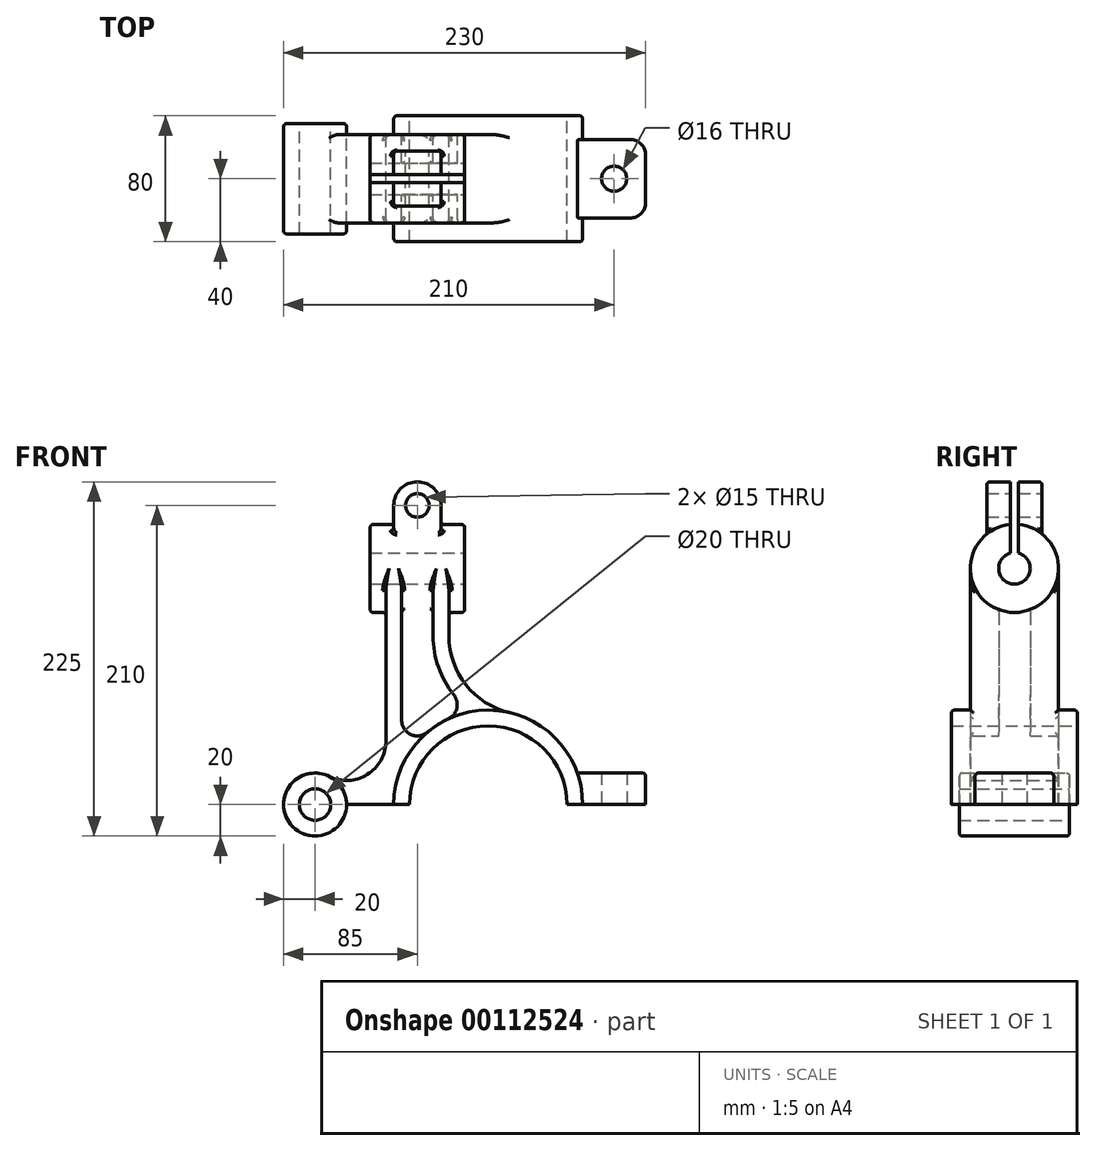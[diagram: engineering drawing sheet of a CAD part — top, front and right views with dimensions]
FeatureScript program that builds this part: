
annotation { "Feature Type Name" : "Feature", "Feature Type Description" : "" }
export const myFeature = defineFeature(function(context is Context, id is Id, definition is map)
    precondition{}
    {
        {
            var Q0;
            Q0=qCreatedBy(makeId("Front.planeOp"),FACE);
            var sketch = newSketch(context, id + "F0", { "sketchPlane" : qUnion([Q0])});
            skLineSegment(sketch, "E0", {"start": v(100, 0) * mm, "end": v(-90, 0) * mm});
            skArc(sketch, "E1", {"start": v(50, 0) * mm, "mid": v(0, 50) * mm, "end": v(-50, 0) * mm});
            skArc(sketch, "E2", {"start": v(60, 0) * mm, "mid": v(0, 60) * mm, "end": v(-60, 0) * mm});
            skLineSegment(sketch, "E3", {"start": v(56.57, 20) * mm, "end": v(100, 20) * mm});
            skLineSegment(sketch, "E4", {"start": v(100, 20) * mm, "end": v(100, 0) * mm});
            skLineSegment(sketch, "E5", {"start": v(80, 20) * mm, "end": v(80, 0) * mm});
            skCircle(sketch, "E6", {"center": v(-110, 0) * mm, "radius": 20 * mm});
            skCircle(sketch, "E7", {"center": v(-110, 0) * mm, "radius": 10 * mm});
            skLineSegment(sketch, "E8", {"start": v(-75, 150) * mm, "end": v(-15, 150) * mm});
            skLineSegment(sketch, "E9", {"start": v(-65, 150) * mm, "end": v(-65, 40.31) * mm});
            skArc(sketch, "E10", {"start": v(-101.11, 17.92) * mm, "mid": v(-76.82, 19.07) * mm, "end": v(-65, 40.31) * mm});
            skLineSegment(sketch, "E11", {"start": v(-25, 150) * mm, "end": v(-25, 107.12) * mm});
            skArc(sketch, "E12", {"start": v(-25, 107.12) * mm, "mid": v(-14.17, 76.04) * mm, "end": v(13.64, 58.43) * mm});
            skLineSegment(sketch, "E13", {"start": v(-35, 150) * mm, "end": v(-35, 107.12) * mm});
            skLineSegment(sketch, "E14", {"start": v(-55, 150) * mm, "end": v(-55, 53.62) * mm});
            skArc(sketch, "E15", {"start": v(-35, 107.12) * mm, "mid": v(-31.62, 87.27) * mm, "end": v(-21.86, 69.65) * mm});
            skArc(sketch, "E16", {"start": v(-55, 53.62) * mm, "mid": v(-49.23, 44.56) * mm, "end": v(-38.57, 45.96) * mm});
            skArc(sketch, "E17", {"start": v(-25.43, 54.34) * mm, "mid": v(-19.93, 61.13) * mm, "end": v(-21.86, 69.65) * mm});
            skLineSegment(sketch, "E18", {"start": v(-75, 178) * mm, "end": v(-75, 122) * mm});
            skLineSegment(sketch, "E19", {"start": v(-75, 122) * mm, "end": v(-15, 122) * mm});
            skLineSegment(sketch, "E20", {"start": v(-15, 122) * mm, "end": v(-15, 178) * mm});
            skLineSegment(sketch, "E21", {"start": v(-15, 178) * mm, "end": v(-75, 178) * mm});
            skLineSegment(sketch, "E22", {"start": v(88, 20) * mm, "end": v(88, 0) * mm});
            skLineSegment(sketch, "E23", {"start": v(-60, 155) * mm, "end": v(-30, 155) * mm});
            skLineSegment(sketch, "E24", {"start": v(-30, 155) * mm, "end": v(-30, 190) * mm});
            skArc(sketch, "E25", {"start": v(-30, 190) * mm, "mid": v(-45, 205) * mm, "end": v(-60, 190) * mm});
            skLineSegment(sketch, "E26", {"start": v(-60, 190) * mm, "end": v(-60, 155) * mm});
            skCircle(sketch, "E27", {"center": v(-45, 190) * mm, "radius": 7.5 * mm});
            skSolve(sketch);
        }
        {
            var Q0;
            {var subQ4=sQuery(id+"F0.wireOp",EDGE,"E1");Q0=makeQuery(id+"F0.imprint","IMPRINT",FACE,{"disambiguationData":[TD([[makeQuery(id+"F0.imprint","IMPRINT",EDGE,{"derivedFrom":subQ4}),-1.0]])]});}
            extrude(context, id + "F1", {"entities" : qUnion([Q0]), "endBound" : BoundingType.SYMMETRIC, "depth" : 80 * mm});
        }
        {
            var Q0;
            Q0=makeQuery(id+"F0.imprint","IMPRINT",FACE,{"disambiguationData":[TD([[makeQuery(id+"F0.imprint","IMPRINT",EDGE,{"derivedFrom":sQuery(id+"F0.wireOp",EDGE,"E7")}),-1.0]])]});
            extrude(context, id + "F2", {"entities" : qUnion([Q0]), "operationType" : NewBodyOperationType.ADD, "endBound" : BoundingType.SYMMETRIC, "depth" : 70 * mm});
        }
        {
            var Q0;
            {var subQ3=sQuery(id+"F0.wireOp",EDGE,"E5");Q0=makeQuery(id+"F0.imprint","IMPRINT",FACE,{"disambiguationData":[TD([[makeQuery(id+"F0.imprint","IMPRINT",EDGE,{"derivedFrom":subQ3}),-1.0]])]});}
            var Q1;
            {var subQ0=sQuery(id+"F0.wireOp",EDGE,"E5");Q1=makeQuery(id+"F0.imprint","IMPRINT",FACE,{"disambiguationData":[TD([[makeQuery(id+"F0.imprint","IMPRINT",EDGE,{"derivedFrom":subQ0}),1.0]])]});}
            var Q2;
            {var subQ0=sQuery(id+"F0.wireOp",EDGE,"E4");Q2=makeQuery(id+"F0.imprint","IMPRINT",FACE,{"disambiguationData":[TD([[makeQuery(id+"F0.imprint","IMPRINT",EDGE,{"derivedFrom":subQ0}),-1.0]])]});}
            extrude(context, id + "F3", {"entities" : qUnion([Q0, Q1, Q2]), "operationType" : NewBodyOperationType.ADD, "endBound" : BoundingType.SYMMETRIC, "depth" : 50 * mm});
        }
        {
            var Q0;
            {var subQ0=sQuery(id+"F0.wireOp",EDGE,"E5");Q0=makeQuery(id+"F0.imprint","IMPRINT",FACE,{"disambiguationData":[TD([[makeQuery(id+"F0.imprint","IMPRINT",EDGE,{"derivedFrom":subQ0}),1.0]])]});}
            var Q1;
            Q1=sQuery(id+"F0.wireOp",EDGE,"E5");
            revolve(context, id + "F4", {"operationType" : NewBodyOperationType.REMOVE, "entities" : qUnion([Q0]), "axis" : qUnion([Q1]), "revolveType" : RevolveType.FULL, "oppositeDirection" : true});
        }
        {
            var Q0;
            Q0=makeQuery(id+"F3.opExtrude","CAP_EDGE",EDGE,{"disambiguationData":[OSD([sQuery(id+"F0.wireOp",EDGE,"E4")])],"isStart":false});
            var Q1;
            Q1=makeQuery(id+"F3.opExtrude","CAP_EDGE",EDGE,{"disambiguationData":[OSD([sQuery(id+"F0.wireOp",EDGE,"E4")])],"isStart":true});
            fillet(context, id + "F5", {"entities" : qUnion([Q0, Q1]), "radius" : 10 * mm, "tangentPropagation" : true, "allowEdgeOverflow" : false});
        }
        {
            var Q0;
            {var subQ3=sQuery(id+"F0.wireOp",EDGE,"E10");Q0=makeQuery(id+"F0.imprint","IMPRINT",FACE,{"disambiguationData":[TD([[makeQuery(id+"F0.imprint","IMPRINT",EDGE,{"derivedFrom":subQ3}),-1.0]])]});}
            var Q1;
            {var subQ0=sQuery(id+"F0.wireOp",EDGE,"E9");var subQ1=sQuery(id+"F0.wireOp",EDGE,"E8");var subQ2=makeQuery(id+"F0.imprint","INTERSECT",VERTEX,{"derivedFrom":[subQ1,subQ0]});Q1=makeQuery(id+"F0.imprint","IMPRINT",FACE,{"disambiguationData":[TD([[makeQuery(id+"F0.imprint","IMPRINT",EDGE,{"disambiguationData":[TD([[subQ2,-1.0]])],"derivedFrom":subQ1}),-1.0]])]});}
            var Q2;
            {var subQ0=sQuery(id+"F0.wireOp",EDGE,"E11");var subQ1=sQuery(id+"F0.wireOp",EDGE,"E8");var subQ2=makeQuery(id+"F0.imprint","INTERSECT",VERTEX,{"derivedFrom":[subQ1,subQ0]});Q2=makeQuery(id+"F0.imprint","IMPRINT",FACE,{"disambiguationData":[TD([[makeQuery(id+"F0.imprint","IMPRINT",EDGE,{"disambiguationData":[TD([[subQ2,1.0]])],"derivedFrom":subQ1}),-1.0]])]});}
            var Q3;
            {var subQ4=sQuery(id+"F0.wireOp",EDGE,"E12");Q3=makeQuery(id+"F0.imprint","IMPRINT",FACE,{"disambiguationData":[TD([[makeQuery(id+"F0.imprint","IMPRINT",EDGE,{"derivedFrom":subQ4}),-1.0]])]});}
            extrude(context, id + "F6", {"entities" : qUnion([Q0, Q1, Q2, Q3]), "operationType" : NewBodyOperationType.ADD, "endBound" : BoundingType.SYMMETRIC, "depth" : 56 * mm});
        }
        {
            var Q0;
            {var subQ0=sQuery(id+"F0.wireOp",EDGE,"E15");Q0=makeQuery(id+"F0.imprint","IMPRINT",FACE,{"disambiguationData":[TD([[makeQuery(id+"F0.imprint","IMPRINT",EDGE,{"derivedFrom":subQ0}),-1.0]])]});}
            var Q1;
            {var subQ0=sQuery(id+"F0.wireOp",EDGE,"E13");var subQ1=sQuery(id+"F0.wireOp",EDGE,"E8");var subQ2=makeQuery(id+"F0.imprint","INTERSECT",VERTEX,{"derivedFrom":[subQ1,subQ0]});Q1=makeQuery(id+"F0.imprint","IMPRINT",FACE,{"disambiguationData":[TD([[makeQuery(id+"F0.imprint","IMPRINT",EDGE,{"disambiguationData":[TD([[subQ2,1.0]])],"derivedFrom":subQ1}),-1.0]])]});}
            extrude(context, id + "F7", {"entities" : qUnion([Q0, Q1]), "operationType" : NewBodyOperationType.ADD, "endBound" : BoundingType.SYMMETRIC, "depth" : 20 * mm});
        }
        {
            var Q0;
            {var subQ11=sQuery(id+"F0.wireOp",EDGE,"E23");Q0=makeQuery(id+"F0.imprint","IMPRINT",FACE,{"disambiguationData":[TD([[makeQuery(id+"F0.imprint","IMPRINT",EDGE,{"derivedFrom":subQ11}),-1.0]])]});}
            var Q1;
            {var subQ5=sQuery(id+"F0.wireOp",EDGE,"E23");Q1=makeQuery(id+"F0.imprint","IMPRINT",FACE,{"disambiguationData":[TD([[makeQuery(id+"F0.imprint","IMPRINT",EDGE,{"derivedFrom":subQ5}),1.0]])]});}
            var Q2;
            Q2=sQuery(id+"F0.wireOp",EDGE,"E8");
            revolve(context, id + "F8", {"operationType" : NewBodyOperationType.ADD, "entities" : qUnion([Q0, Q1]), "axis" : qUnion([Q2]), "revolveType" : RevolveType.FULL});
        }
        {
            var Q0;
            {var subQ1=sQuery(id+"F0.wireOp",EDGE,"E25");Q0=makeQuery(id+"F0.imprint","IMPRINT",FACE,{"disambiguationData":[TD([[makeQuery(id+"F0.imprint","IMPRINT",EDGE,{"derivedFrom":subQ1}),1.0]])]});}
            var Q1;
            {var subQ5=sQuery(id+"F0.wireOp",EDGE,"E23");Q1=makeQuery(id+"F0.imprint","IMPRINT",FACE,{"disambiguationData":[TD([[makeQuery(id+"F0.imprint","IMPRINT",EDGE,{"derivedFrom":subQ5}),1.0]])]});}
            extrude(context, id + "F9", {"entities" : qUnion([Q0, Q1]), "operationType" : NewBodyOperationType.ADD, "endBound" : BoundingType.SYMMETRIC, "depth" : 35 * mm});
        }
        {
            var Q0;
            Q0=makeQuery(id+"F8.opRevolve","SWEPT_FACE",FACE,{"disambiguationData":[OSD([sQuery(id+"F0.wireOp",EDGE,"E20")])]});
            var sketch = newSketch(context, id + "F10", { "sketchPlane" : qUnion([Q0])});
            skCircle(sketch, "E28", {"center": v(0, 150) * mm, "radius": 10 * mm});
            skSolve(sketch);
        }
        {
            var Q0;
            Q0 = qSketchRegion(id + "F10", true);
            extrude(context, id + "F11", {"entities" : qUnion([Q0]), "operationType" : NewBodyOperationType.REMOVE, "endBound" : BoundingType.UP_TO_NEXT, "oppositeDirection" : true, "depth" : 25 * mm});
        }
        {
            var Q0;
            {var subQ5=sQuery(id+"F0.wireOp",EDGE,"E23");Q0=makeQuery(id+"F0.imprint","IMPRINT",FACE,{"disambiguationData":[TD([[makeQuery(id+"F0.imprint","IMPRINT",EDGE,{"derivedFrom":subQ5}),1.0]])]});}
            var Q1;
            {var subQ1=sQuery(id+"F0.wireOp",EDGE,"E25");Q1=makeQuery(id+"F0.imprint","IMPRINT",FACE,{"disambiguationData":[TD([[makeQuery(id+"F0.imprint","IMPRINT",EDGE,{"derivedFrom":subQ1}),1.0]])]});}
            var Q2;
            {var subQ11=sQuery(id+"F0.wireOp",EDGE,"E23");Q2=makeQuery(id+"F0.imprint","IMPRINT",FACE,{"disambiguationData":[TD([[makeQuery(id+"F0.imprint","IMPRINT",EDGE,{"derivedFrom":subQ11}),-1.0]])]});}
            extrude(context, id + "F12", {"entities" : qUnion([Q0, Q1, Q2]), "operationType" : NewBodyOperationType.REMOVE, "endBound" : BoundingType.SYMMETRIC, "oppositeDirection" : true, "depth" : 5 * mm});
        }
        {
            var Q0;
            Q0=makeQuery(id+"F7.opExtrude","CAP_EDGE",EDGE,{"disambiguationData":[OSD([sQuery(id+"F0.wireOp",EDGE,"E14")])],"isStart":false});
            var Q1;
            Q1=makeQuery(id+"F8.boolean.opBoolean","INTERSECT",EDGE,{"derivedFrom":[makeQuery(id+"F7.opExtrude","CAP_FACE",FACE,{"disambiguationData":[OSD([sQuery(id+"F0.wireOp",EDGE,"E2"),sQuery(id+"F0.wireOp",EDGE,"E8"),sQuery(id+"F0.wireOp",EDGE,"E13"),sQuery(id+"F0.wireOp",EDGE,"E14"),sQuery(id+"F0.wireOp",EDGE,"E15"),sQuery(id+"F0.wireOp",EDGE,"E16"),sQuery(id+"F0.wireOp",EDGE,"E17")])],"isStart":false}),makeQuery(id+"F8.opRevolve","SWEPT_FACE",FACE,{"disambiguationData":[OSD([sQuery(id+"F0.wireOp",EDGE,"E21")])]})]});
            var Q2;
            {var subQ0=sQuery(id+"F0.wireOp",EDGE,"E15");var subQ1=sQuery(id+"F0.wireOp",EDGE,"E11");var subQ2=sQuery(id+"F0.wireOp",EDGE,"E8");var subQ3=sQuery(id+"F0.wireOp",EDGE,"E13");var subQ5=sQuery(id+"F0.wireOp",EDGE,"E17");var subQ6=sQuery(id+"F0.wireOp",EDGE,"E2");Q2=makeQuery(id+"F8.boolean.opBoolean","INTERSECT",EDGE,{"derivedFrom":[makeQuery(id+"F7.boolean.opBoolean","SPLIT",FACE,{"disambiguationData":[TD([makeQuery(id+"F6.opExtrude","CAP_FACE",FACE,{"disambiguationData":[OSD([subQ6,subQ2,subQ1,sQuery(id+"F0.wireOp",EDGE,"E12"),subQ3,subQ0,subQ5])],"isStart":false})])],"derivedFrom":makeQuery(id+"F6.opExtrude","SWEPT_FACE",FACE,{"disambiguationData":[OSD([subQ3])]})}),makeQuery(id+"F8.opRevolve","SWEPT_FACE",FACE,{"disambiguationData":[OSD([sQuery(id+"F0.wireOp",EDGE,"E21")])]})]});}
            var Q3;
            {var subQ0=sQuery(id+"F0.wireOp",EDGE,"E16");var subQ1=sQuery(id+"F0.wireOp",EDGE,"E8");var subQ2=sQuery(id+"F0.wireOp",EDGE,"E13");var subQ3=sQuery(id+"F0.wireOp",EDGE,"E14");var subQ5=sQuery(id+"F0.wireOp",EDGE,"E2");Q3=makeQuery(id+"F8.boolean.opBoolean","INTERSECT",EDGE,{"derivedFrom":[makeQuery(id+"F7.boolean.opBoolean","SPLIT",FACE,{"disambiguationData":[TD([makeQuery(id+"F7.opExtrude","CAP_FACE",FACE,{"disambiguationData":[OSD([subQ5,subQ1,subQ2,subQ3,sQuery(id+"F0.wireOp",EDGE,"E15"),subQ0,sQuery(id+"F0.wireOp",EDGE,"E17")])],"isStart":false})])],"derivedFrom":makeQuery(id+"F6.opExtrude","SWEPT_FACE",FACE,{"disambiguationData":[OSD([subQ3])]})}),makeQuery(id+"F8.opRevolve","SWEPT_FACE",FACE,{"disambiguationData":[OSD([sQuery(id+"F0.wireOp",EDGE,"E21")])]})]});}
            var Q4;
            Q4=makeQuery(id+"F8.boolean.opBoolean","INTERSECT",EDGE,{"derivedFrom":[makeQuery(id+"F6.opExtrude","SWEPT_FACE",FACE,{"disambiguationData":[OSD([sQuery(id+"F0.wireOp",EDGE,"E9")])]}),makeQuery(id+"F8.opRevolve","SWEPT_FACE",FACE,{"disambiguationData":[OSD([sQuery(id+"F0.wireOp",EDGE,"E21")])]})]});
            var Q5;
            Q5=makeQuery(id+"F8.boolean.opBoolean","INTERSECT",EDGE,{"derivedFrom":[makeQuery(id+"F6.opExtrude","SWEPT_FACE",FACE,{"disambiguationData":[OSD([sQuery(id+"F0.wireOp",EDGE,"E11")])]}),makeQuery(id+"F8.opRevolve","SWEPT_FACE",FACE,{"disambiguationData":[OSD([sQuery(id+"F0.wireOp",EDGE,"E21")])]})]});
            var Q6;
            {var subQ0=sQuery(id+"F0.wireOp",EDGE,"E2");Q6=makeQuery(id+"F6.opExtrude","CAP_EDGE",EDGE,{"disambiguationData":[OSD([subQ0]),TDD([makeQuery(id+"F0.imprint","IMPRINT",EDGE,{"disambiguationData":[TD([[makeQuery(id+"F0.imprint","INTERSECT",VERTEX,{"derivedFrom":[subQ0,sQuery(id+"F0.wireOp",EDGE,"E12")]}),-1.0]])],"derivedFrom":subQ0})])],"isStart":false});}
            var Q7;
            {var subQ0=sQuery(id+"F0.wireOp",EDGE,"E2");Q7=makeQuery(id+"F6.opExtrude","CAP_EDGE",EDGE,{"disambiguationData":[OSD([subQ0]),TDD([makeQuery(id+"F0.imprint","IMPRINT",EDGE,{"disambiguationData":[TD([[makeQuery(id+"F0.imprint","INTERSECT",VERTEX,{"disambiguationData":[OD(1.0)],"derivedFrom":[sQuery(id+"F0.wireOp",EDGE,"E0"),subQ0]}),1.0]])],"derivedFrom":subQ0})])],"isStart":false});}
            var Q8;
            {var subQ0=sQuery(id+"F0.wireOp",EDGE,"E2");Q8=makeQuery(id+"F6.opExtrude","CAP_EDGE",EDGE,{"disambiguationData":[OSD([subQ0]),TDD([makeQuery(id+"F0.imprint","IMPRINT",EDGE,{"disambiguationData":[TD([[makeQuery(id+"F0.imprint","INTERSECT",VERTEX,{"derivedFrom":[subQ0,sQuery(id+"F0.wireOp",EDGE,"E12")]}),-1.0]])],"derivedFrom":subQ0})])],"isStart":true});}
            var Q9;
            {var subQ0=sQuery(id+"F0.wireOp",EDGE,"E2");Q9=makeQuery(id+"F6.opExtrude","CAP_EDGE",EDGE,{"disambiguationData":[OSD([subQ0]),TDD([makeQuery(id+"F0.imprint","IMPRINT",EDGE,{"disambiguationData":[TD([[makeQuery(id+"F0.imprint","INTERSECT",VERTEX,{"disambiguationData":[OD(1.0)],"derivedFrom":[sQuery(id+"F0.wireOp",EDGE,"E0"),subQ0]}),1.0]])],"derivedFrom":subQ0})])],"isStart":true});}
            var Q10;
            Q10=makeQuery(id+"F7.opExtrude","CAP_EDGE",EDGE,{"disambiguationData":[OSD([sQuery(id+"F0.wireOp",EDGE,"E2")])],"isStart":true});
            var Q11;
            Q11=makeQuery(id+"F8.boolean.opBoolean","INTERSECT",EDGE,{"derivedFrom":[makeQuery(id+"F7.opExtrude","CAP_FACE",FACE,{"disambiguationData":[OSD([sQuery(id+"F0.wireOp",EDGE,"E2"),sQuery(id+"F0.wireOp",EDGE,"E8"),sQuery(id+"F0.wireOp",EDGE,"E13"),sQuery(id+"F0.wireOp",EDGE,"E14"),sQuery(id+"F0.wireOp",EDGE,"E15"),sQuery(id+"F0.wireOp",EDGE,"E16"),sQuery(id+"F0.wireOp",EDGE,"E17")])],"isStart":true}),makeQuery(id+"F8.opRevolve","SWEPT_FACE",FACE,{"disambiguationData":[OSD([sQuery(id+"F0.wireOp",EDGE,"E21")])]})]});
            var Q12;
            {var subQ0=sQuery(id+"F0.wireOp",EDGE,"E16");var subQ1=sQuery(id+"F0.wireOp",EDGE,"E8");var subQ2=sQuery(id+"F0.wireOp",EDGE,"E13");var subQ4=sQuery(id+"F0.wireOp",EDGE,"E14");var subQ5=sQuery(id+"F0.wireOp",EDGE,"E2");Q12=makeQuery(id+"F8.boolean.opBoolean","INTERSECT",EDGE,{"derivedFrom":[makeQuery(id+"F7.boolean.opBoolean","SPLIT",FACE,{"disambiguationData":[TD([makeQuery(id+"F7.opExtrude","CAP_FACE",FACE,{"disambiguationData":[OSD([subQ5,subQ1,subQ2,subQ4,sQuery(id+"F0.wireOp",EDGE,"E15"),subQ0,sQuery(id+"F0.wireOp",EDGE,"E17")])],"isStart":true})])],"derivedFrom":makeQuery(id+"F6.opExtrude","SWEPT_FACE",FACE,{"disambiguationData":[OSD([subQ4])]})}),makeQuery(id+"F8.opRevolve","SWEPT_FACE",FACE,{"disambiguationData":[OSD([sQuery(id+"F0.wireOp",EDGE,"E21")])]})]});}
            var Q13;
            {var subQ0=sQuery(id+"F0.wireOp",EDGE,"E15");var subQ1=sQuery(id+"F0.wireOp",EDGE,"E11");var subQ2=sQuery(id+"F0.wireOp",EDGE,"E8");var subQ3=sQuery(id+"F0.wireOp",EDGE,"E13");var subQ5=sQuery(id+"F0.wireOp",EDGE,"E17");var subQ6=sQuery(id+"F0.wireOp",EDGE,"E2");Q13=makeQuery(id+"F8.boolean.opBoolean","INTERSECT",EDGE,{"derivedFrom":[makeQuery(id+"F7.boolean.opBoolean","SPLIT",FACE,{"disambiguationData":[TD([makeQuery(id+"F6.opExtrude","CAP_FACE",FACE,{"disambiguationData":[OSD([subQ6,subQ2,subQ1,sQuery(id+"F0.wireOp",EDGE,"E12"),subQ3,subQ0,subQ5])],"isStart":true})])],"derivedFrom":makeQuery(id+"F6.opExtrude","SWEPT_FACE",FACE,{"disambiguationData":[OSD([subQ3])]})}),makeQuery(id+"F8.opRevolve","SWEPT_FACE",FACE,{"disambiguationData":[OSD([sQuery(id+"F0.wireOp",EDGE,"E21")])]})]});}
            var Q14;
            Q14=makeQuery(id+"F6.opExtrude","CAP_EDGE",EDGE,{"disambiguationData":[OSD([sQuery(id+"F0.wireOp",EDGE,"E6")])],"isStart":true});
            var Q15;
            Q15=makeQuery(id+"F6.opExtrude","CAP_EDGE",EDGE,{"disambiguationData":[OSD([sQuery(id+"F0.wireOp",EDGE,"E6")])],"isStart":false});
            var Q16;
            Q16=makeQuery(id+"F6.opExtrude","SWEPT_EDGE",EDGE,{"disambiguationData":[OSD([sQuery(id+"F0.wireOp",EDGE,"E0"),sQuery(id+"F0.wireOp",EDGE,"E6")])]});
            var Q17;
            Q17=makeQuery(id+"F9.boolean.opBoolean","INTERSECT",EDGE,{"derivedFrom":[makeQuery(id+"F8.opRevolve","SWEPT_FACE",FACE,{"disambiguationData":[OSD([sQuery(id+"F0.wireOp",EDGE,"E21")])]}),makeQuery(id+"F9.opExtrude","CAP_FACE",FACE,{"disambiguationData":[OSD([sQuery(id+"F0.wireOp",EDGE,"E23"),sQuery(id+"F0.wireOp",EDGE,"E24"),sQuery(id+"F0.wireOp",EDGE,"E25"),sQuery(id+"F0.wireOp",EDGE,"E26"),sQuery(id+"F0.wireOp",EDGE,"E27")])],"isStart":true})]});
            var Q18;
            {var subQ0=sQuery(id+"F0.wireOp",EDGE,"E21");var subQ1=makeQuery(id+"F8.opRevolve","SWEPT_FACE",FACE,{"disambiguationData":[OSD([subQ0])]});var subQ2=sQuery(id+"F0.wireOp",EDGE,"E27");var subQ3=sQuery(id+"F0.wireOp",EDGE,"E26");var subQ4=sQuery(id+"F0.wireOp",EDGE,"E25");var subQ5=sQuery(id+"F0.wireOp",EDGE,"E24");var subQ6=makeQuery(id+"F9.opExtrude","SWEPT_FACE",FACE,{"disambiguationData":[OSD([subQ3])]});Q18=makeQuery(id+"F12.boolean.opBoolean","SPLIT",EDGE,{"disambiguationData":[TD([makeQuery(id+"F9.opExtrude","CAP_FACE",FACE,{"disambiguationData":[OSD([sQuery(id+"F0.wireOp",EDGE,"E23"),subQ5,subQ4,subQ3,subQ2])],"isStart":true})])],"derivedFrom":makeQuery(id+"F9.boolean.opBoolean","INTERSECT",EDGE,{"derivedFrom":[subQ1,subQ6]})});}
            var Q19;
            Q19=makeQuery(id+"F9.boolean.opBoolean","INTERSECT",EDGE,{"derivedFrom":[makeQuery(id+"F8.opRevolve","SWEPT_FACE",FACE,{"disambiguationData":[OSD([sQuery(id+"F0.wireOp",EDGE,"E21")])]}),makeQuery(id+"F9.opExtrude","CAP_FACE",FACE,{"disambiguationData":[OSD([sQuery(id+"F0.wireOp",EDGE,"E23"),sQuery(id+"F0.wireOp",EDGE,"E24"),sQuery(id+"F0.wireOp",EDGE,"E25"),sQuery(id+"F0.wireOp",EDGE,"E26"),sQuery(id+"F0.wireOp",EDGE,"E27")])],"isStart":false})]});
            var Q20;
            {var subQ0=sQuery(id+"F0.wireOp",EDGE,"E21");var subQ1=makeQuery(id+"F8.opRevolve","SWEPT_FACE",FACE,{"disambiguationData":[OSD([subQ0])]});var subQ2=sQuery(id+"F0.wireOp",EDGE,"E27");var subQ3=sQuery(id+"F0.wireOp",EDGE,"E26");var subQ4=sQuery(id+"F0.wireOp",EDGE,"E25");var subQ5=sQuery(id+"F0.wireOp",EDGE,"E24");var subQ6=makeQuery(id+"F9.opExtrude","SWEPT_FACE",FACE,{"disambiguationData":[OSD([subQ3])]});Q20=makeQuery(id+"F12.boolean.opBoolean","SPLIT",EDGE,{"disambiguationData":[TD([makeQuery(id+"F9.opExtrude","CAP_FACE",FACE,{"disambiguationData":[OSD([sQuery(id+"F0.wireOp",EDGE,"E23"),subQ5,subQ4,subQ3,subQ2])],"isStart":false})])],"derivedFrom":makeQuery(id+"F9.boolean.opBoolean","INTERSECT",EDGE,{"derivedFrom":[subQ1,subQ6]})});}
            var Q21;
            {var subQ0=sQuery(id+"F0.wireOp",EDGE,"E21");var subQ1=makeQuery(id+"F8.opRevolve","SWEPT_FACE",FACE,{"disambiguationData":[OSD([subQ0])]});var subQ2=sQuery(id+"F0.wireOp",EDGE,"E27");var subQ3=sQuery(id+"F0.wireOp",EDGE,"E26");var subQ4=sQuery(id+"F0.wireOp",EDGE,"E25");var subQ5=sQuery(id+"F0.wireOp",EDGE,"E24");var subQ6=makeQuery(id+"F9.opExtrude","SWEPT_FACE",FACE,{"disambiguationData":[OSD([subQ5])]});Q21=makeQuery(id+"F12.boolean.opBoolean","SPLIT",EDGE,{"disambiguationData":[TD([makeQuery(id+"F9.opExtrude","CAP_FACE",FACE,{"disambiguationData":[OSD([sQuery(id+"F0.wireOp",EDGE,"E23"),subQ5,subQ4,subQ3,subQ2])],"isStart":false})])],"derivedFrom":makeQuery(id+"F9.boolean.opBoolean","INTERSECT",EDGE,{"derivedFrom":[subQ1,subQ6]})});}
            var Q22;
            {var subQ0=sQuery(id+"F0.wireOp",EDGE,"E21");var subQ1=makeQuery(id+"F8.opRevolve","SWEPT_FACE",FACE,{"disambiguationData":[OSD([subQ0])]});var subQ2=sQuery(id+"F0.wireOp",EDGE,"E27");var subQ3=sQuery(id+"F0.wireOp",EDGE,"E26");var subQ4=sQuery(id+"F0.wireOp",EDGE,"E25");var subQ5=sQuery(id+"F0.wireOp",EDGE,"E24");var subQ6=makeQuery(id+"F9.opExtrude","SWEPT_FACE",FACE,{"disambiguationData":[OSD([subQ5])]});Q22=makeQuery(id+"F12.boolean.opBoolean","SPLIT",EDGE,{"disambiguationData":[TD([makeQuery(id+"F9.opExtrude","CAP_FACE",FACE,{"disambiguationData":[OSD([sQuery(id+"F0.wireOp",EDGE,"E23"),subQ5,subQ4,subQ3,subQ2])],"isStart":true})])],"derivedFrom":makeQuery(id+"F9.boolean.opBoolean","INTERSECT",EDGE,{"derivedFrom":[subQ1,subQ6]})});}
            var Q23;
            Q23=makeQuery(id+"F9.opExtrude","CAP_EDGE",EDGE,{"disambiguationData":[OSD([sQuery(id+"F0.wireOp",EDGE,"E24")])],"isStart":false});
            var Q24;
            Q24=makeQuery(id+"F9.opExtrude","CAP_EDGE",EDGE,{"disambiguationData":[OSD([sQuery(id+"F0.wireOp",EDGE,"E24")])],"isStart":true});
            var Q25;
            Q25=makeQuery(id+"F8.opRevolve","SWEPT_EDGE",EDGE,{"disambiguationData":[OSD([sQuery(id+"F0.wireOp",EDGE,"E20"),sQuery(id+"F0.wireOp",EDGE,"E21")])]});
            var Q26;
            Q26=makeQuery(id+"F8.opRevolve","SWEPT_EDGE",EDGE,{"disambiguationData":[OSD([sQuery(id+"F0.wireOp",EDGE,"E18"),sQuery(id+"F0.wireOp",EDGE,"E21")])]});
            var Q27;
            Q27=makeQuery(id+"F3.opExtrude","CAP_EDGE",EDGE,{"disambiguationData":[OSD([sQuery(id+"F0.wireOp",EDGE,"E2")])],"isStart":true});
            var Q28;
            Q28=makeQuery(id+"F3.opExtrude","SWEPT_EDGE",EDGE,{"disambiguationData":[OSD([sQuery(id+"F0.wireOp",EDGE,"E2"),sQuery(id+"F0.wireOp",EDGE,"E3")])]});
            var Q29;
            Q29=makeQuery(id+"F3.opExtrude","CAP_EDGE",EDGE,{"disambiguationData":[OSD([sQuery(id+"F0.wireOp",EDGE,"E2")])],"isStart":false});
            var Q30;
            Q30=makeQuery(id+"F3.opExtrude","CAP_EDGE",EDGE,{"disambiguationData":[OSD([sQuery(id+"F0.wireOp",EDGE,"E3")])],"isStart":false});
            var Q31;
            Q31=makeQuery(id+"F2.opExtrude","CAP_EDGE",EDGE,{"disambiguationData":[OSD([sQuery(id+"F0.wireOp",EDGE,"E6")])],"isStart":true});
            var Q32;
            Q32=makeQuery(id+"F2.opExtrude","CAP_EDGE",EDGE,{"disambiguationData":[OSD([sQuery(id+"F0.wireOp",EDGE,"E6")])],"isStart":false});
            var Q33;
            Q33=makeQuery(id+"F6.opExtrude","CAP_EDGE",EDGE,{"disambiguationData":[OSD([sQuery(id+"F0.wireOp",EDGE,"E10")])],"isStart":false});
            var Q34;
            Q34=makeQuery(id+"F6.opExtrude","CAP_EDGE",EDGE,{"disambiguationData":[OSD([sQuery(id+"F0.wireOp",EDGE,"E10")])],"isStart":true});
            var Q35;
            Q35=makeQuery(id+"F6.opExtrude","CAP_EDGE",EDGE,{"disambiguationData":[OSD([sQuery(id+"F0.wireOp",EDGE,"E12")])],"isStart":true});
            var Q36;
            Q36=makeQuery(id+"F6.opExtrude","CAP_EDGE",EDGE,{"disambiguationData":[OSD([sQuery(id+"F0.wireOp",EDGE,"E12")])],"isStart":false});
            var Q37;
            Q37=makeQuery(id+"F6.opExtrude","CAP_EDGE",EDGE,{"disambiguationData":[OSD([sQuery(id+"F0.wireOp",EDGE,"E16")])],"isStart":false});
            var Q38;
            Q38=makeQuery(id+"F6.opExtrude","CAP_EDGE",EDGE,{"disambiguationData":[OSD([sQuery(id+"F0.wireOp",EDGE,"E17")])],"isStart":false});
            var Q39;
            Q39=makeQuery(id+"F6.opExtrude","CAP_EDGE",EDGE,{"disambiguationData":[OSD([sQuery(id+"F0.wireOp",EDGE,"E14")])],"isStart":true});
            var Q40;
            Q40=makeQuery(id+"F6.opExtrude","CAP_EDGE",EDGE,{"disambiguationData":[OSD([sQuery(id+"F0.wireOp",EDGE,"E17")])],"isStart":true});
            var Q41;
            Q41=makeQuery(id+"F1.opExtrude","CAP_EDGE",EDGE,{"disambiguationData":[OSD([sQuery(id+"F0.wireOp",EDGE,"E2")])],"isStart":true});
            var Q42;
            Q42=makeQuery(id+"F1.opExtrude","CAP_EDGE",EDGE,{"disambiguationData":[OSD([sQuery(id+"F0.wireOp",EDGE,"E2")])],"isStart":false});
            fillet(context, id + "F13", {"entities" : qUnion([Q0, Q1, Q2, Q3, Q4, Q5, Q6, Q7, Q8, Q9, Q10, Q11, Q12, Q13, Q14, Q15, Q16, Q17, Q18, Q19, Q20, Q21, Q22, Q23, Q24, Q25, Q26, Q27, Q28, Q29, Q30, Q31, Q32, Q33, Q34, Q35, Q36, Q37, Q38, Q39, Q40, Q41, Q42]), "radius" : 2 * mm, "tangentPropagation" : true, "allowEdgeOverflow" : false});
        }
    });
